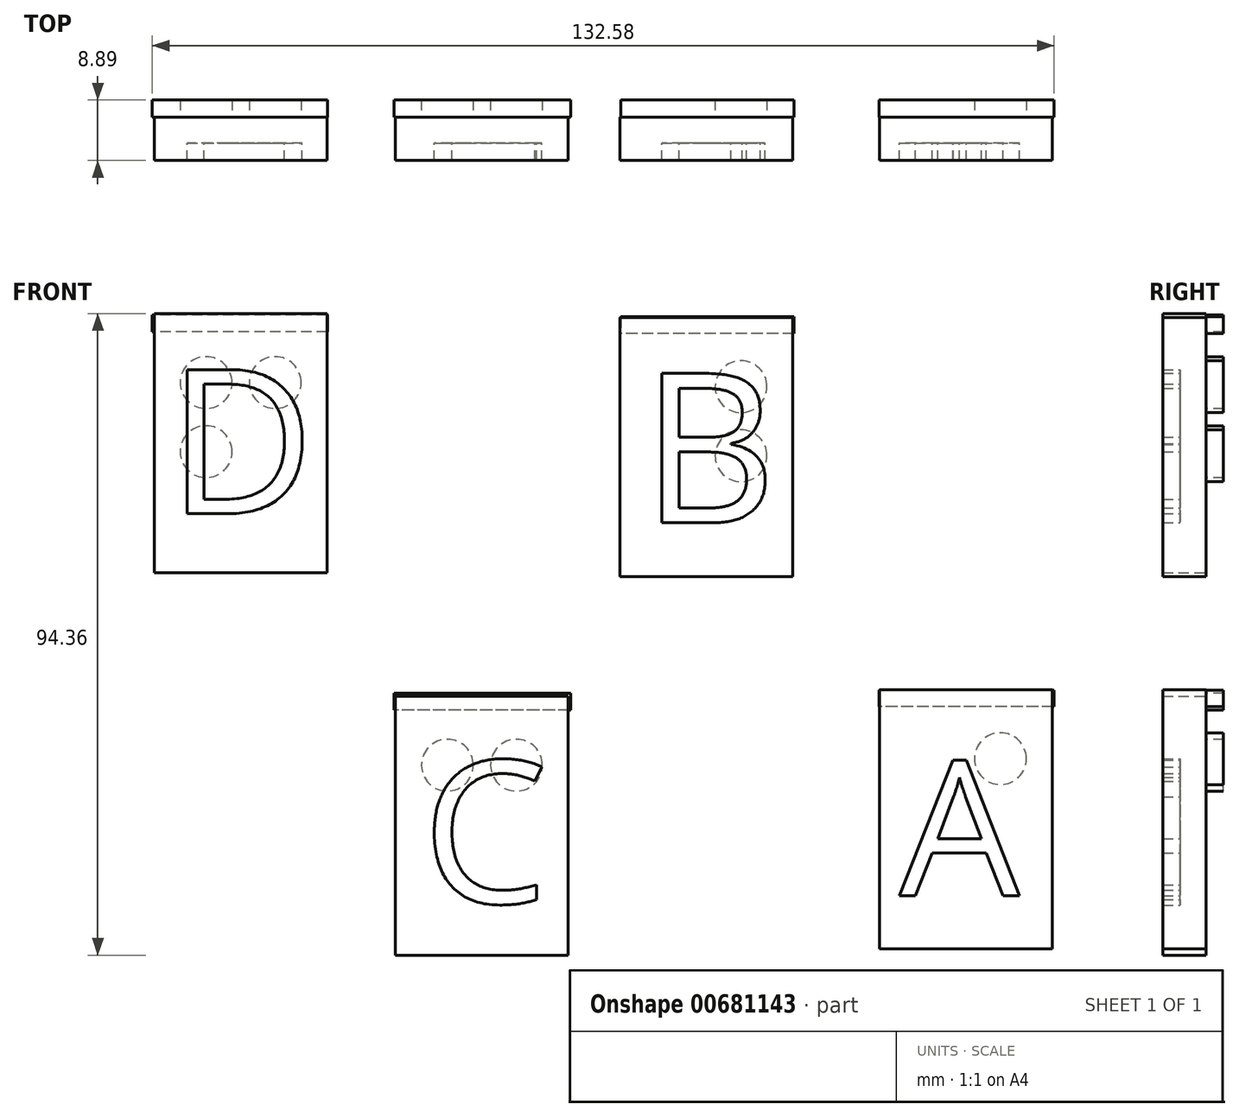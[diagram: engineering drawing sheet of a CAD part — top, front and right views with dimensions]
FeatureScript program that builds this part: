
annotation { "Feature Type Name" : "Feature", "Feature Type Description" : "" }
export const myFeature = defineFeature(function(context is Context, id is Id, definition is map)
    precondition{}
    {
        {
            var Q0;
            Q0=qCreatedBy(makeId("Front.planeOp"),FACE);
            var sketch = newSketch(context, id + "F0", { "sketchPlane" : qUnion([Q0])});
            skLineSegment(sketch, "E0.bottom", {"start": v(-58.76, 38.35) * mm, "end": v(-33.36, 38.35) * mm});
            skLineSegment(sketch, "E0.top", {"start": v(-58.76, 0.25) * mm, "end": v(-33.36, 0.25) * mm});
            skLineSegment(sketch, "E0.left", {"start": v(-58.76, 38.35) * mm, "end": v(-58.76, 0.25) * mm});
            skLineSegment(sketch, "E0.right", {"start": v(-33.36, 38.35) * mm, "end": v(-33.36, 0.25) * mm});
            skLineSegment(sketch, "E1.bottom", {"start": v(-23.3, -17.91) * mm, "end": v(2.1, -17.91) * mm});
            skLineSegment(sketch, "E1.top", {"start": v(-23.3, -56.01) * mm, "end": v(2.1, -56.01) * mm});
            skLineSegment(sketch, "E1.left", {"start": v(-23.3, -17.91) * mm, "end": v(-23.3, -56.01) * mm});
            skLineSegment(sketch, "E1.right", {"start": v(2.1, -17.91) * mm, "end": v(2.1, -56.01) * mm});
            skLineSegment(sketch, "E2.bottom", {"start": v(47.85, -16.96) * mm, "end": v(73.25, -16.96) * mm});
            skLineSegment(sketch, "E2.top", {"start": v(47.85, -55.06) * mm, "end": v(73.25, -55.06) * mm});
            skLineSegment(sketch, "E2.left", {"start": v(47.85, -16.96) * mm, "end": v(47.85, -55.06) * mm});
            skLineSegment(sketch, "E2.right", {"start": v(73.25, -16.96) * mm, "end": v(73.25, -55.06) * mm});
            skLineSegment(sketch, "E3.bottom", {"start": v(9.7, 37.75) * mm, "end": v(35.1, 37.75) * mm});
            skLineSegment(sketch, "E3.top", {"start": v(9.7, -0.35) * mm, "end": v(35.1, -0.35) * mm});
            skLineSegment(sketch, "E3.left", {"start": v(9.7, 37.75) * mm, "end": v(9.7, -0.35) * mm});
            skLineSegment(sketch, "E3.right", {"start": v(35.1, 37.75) * mm, "end": v(35.1, -0.35) * mm});
            skSolve(sketch);
        }
        {
            var Q0;
            Q0=qSketchRegion(id+"F0",true);
            extrude(context, id + "F1", {"entities" : qUnion([Q0]), "depth" : 6.35 * mm});
        }
        {
            var Q0;
            Q0=qCreatedBy(makeId("Front.planeOp"),FACE);
            var sketch = newSketch(context, id + "F2", { "sketchPlane" : qUnion([Q0])});
            skCircle(sketch, "E4", {"center": v(27.49, 17.43) * mm, "radius": 3.81 * mm});
            skCircle(sketch, "E5", {"center": v(65.63, -27.12) * mm, "radius": 3.81 * mm});
            skCircle(sketch, "E6", {"center": v(-5.52, -28.07) * mm, "radius": 3.81 * mm});
            skCircle(sketch, "E7", {"center": v(-15.68, -28.07) * mm, "radius": 3.81 * mm});
            skCircle(sketch, "E8", {"center": v(27.49, 27.59) * mm, "radius": 3.81 * mm});
            skCircle(sketch, "E9", {"center": v(-40.98, 28.19) * mm, "radius": 3.81 * mm});
            skCircle(sketch, "E10", {"center": v(-51.14, 28.19) * mm, "radius": 3.81 * mm});
            skCircle(sketch, "E11", {"center": v(-51.14, 18.03) * mm, "radius": 3.81 * mm});
            skSolve(sketch);
        }
        {
            var Q0;
            Q0=qSketchRegion(id+"F2",true);
            extrude(context, id + "F3", {"entities" : qUnion([Q0]), "operationType" : NewBodyOperationType.ADD, "oppositeDirection" : true, "depth" : 2.54 * mm});
        }
        {
            var Q0;
            Q0=qCreatedBy(makeId("Front.planeOp"),FACE);
            cPlane(context, id + "F4", {"entities" : qUnion([Q0]), "cplaneType" : CPlaneType.OFFSET, "offset" : 3.8 * mm, "width" : 152.4 * mm, "height" : 152.4 * mm});
        }
        {
            var Q0;
            Q0=qCreatedBy(id+"F4.planeOp",FACE);
            var sketch = newSketch(context, id + "F5", { "sketchPlane" : qUnion([Q0])});
            skText(sketch, "E12", { "text": "A", "fontName": "OpenSans-Regular.ttf"});
            skText(sketch, "E13", { "text": "B", "fontName": "OpenSans-Regular.ttf"});
            skText(sketch, "E14", { "text": "C", "fontName": "OpenSans-Regular.ttf"});
            skText(sketch, "E15", { "text": "D", "fontName": "OpenSans-Regular.ttf"});
            const initialGuessF5  = {"E12": [0.0508, -0.0473, 1, 0, 0.02005], "E13": [0.0128, 0.00758, 1, 0, 0.02216], "E14": [-0.01939, -0.04835, 1, 0, 0.0211], "E15": [-0.05685, 0.0089, 1, 0, 0.02137]};
            skSetInitialGuess(sketch, initialGuessF5);
            skSolve(sketch);
        }
        {
            var Q0;
            Q0=qSketchRegion(id+"F5",true);
            extrude(context, id + "F6", {"entities" : qUnion([Q0]), "operationType" : NewBodyOperationType.REMOVE, "depth" : 25.4 * mm});
        }
        {
            var Q0;
            Q0=qCreatedBy(makeId("Front.planeOp"),FACE);
            var sketch = newSketch(context, id + "F7", { "sketchPlane" : qUnion([Q0])});
            skLineSegment(sketch, "E16.bottom", {"start": v(73.52, -17.03) * mm, "end": v(47.79, -17.03) * mm});
            skLineSegment(sketch, "E16.top", {"start": v(73.52, -19.48) * mm, "end": v(47.79, -19.48) * mm});
            skLineSegment(sketch, "E16.left", {"start": v(73.52, -17.03) * mm, "end": v(73.52, -19.48) * mm});
            skLineSegment(sketch, "E16.right", {"start": v(47.79, -17.03) * mm, "end": v(47.79, -19.48) * mm});
            skLineSegment(sketch, "E17.bottom", {"start": v(35.29, 37.86) * mm, "end": v(9.8, 37.86) * mm});
            skLineSegment(sketch, "E17.top", {"start": v(35.29, 35.41) * mm, "end": v(9.8, 35.41) * mm});
            skLineSegment(sketch, "E17.left", {"start": v(35.29, 37.86) * mm, "end": v(35.29, 35.41) * mm});
            skLineSegment(sketch, "E17.right", {"start": v(9.8, 37.86) * mm, "end": v(9.8, 35.41) * mm});
            skLineSegment(sketch, "E18.bottom", {"start": v(-33.33, 38.1) * mm, "end": v(-59.06, 38.1) * mm});
            skLineSegment(sketch, "E18.top", {"start": v(-33.33, 35.66) * mm, "end": v(-59.06, 35.66) * mm});
            skLineSegment(sketch, "E18.left", {"start": v(-33.33, 38.1) * mm, "end": v(-33.33, 35.66) * mm});
            skLineSegment(sketch, "E18.right", {"start": v(-59.06, 38.1) * mm, "end": v(-59.06, 35.66) * mm});
            skLineSegment(sketch, "E19.bottom", {"start": v(2.45, -17.52) * mm, "end": v(-23.53, -17.52) * mm});
            skLineSegment(sketch, "E19.top", {"start": v(2.45, -19.97) * mm, "end": v(-23.53, -19.97) * mm});
            skLineSegment(sketch, "E19.left", {"start": v(2.45, -17.52) * mm, "end": v(2.45, -19.97) * mm});
            skLineSegment(sketch, "E19.right", {"start": v(-23.53, -17.52) * mm, "end": v(-23.53, -19.97) * mm});
            skSolve(sketch);
        }
        {
            var Q0;
            Q0=qSketchRegion(id+"F7",true);
            extrude(context, id + "F8", {"entities" : qUnion([Q0]), "operationType" : NewBodyOperationType.ADD, "oppositeDirection" : true, "depth" : 2.54 * mm});
        }
    });
